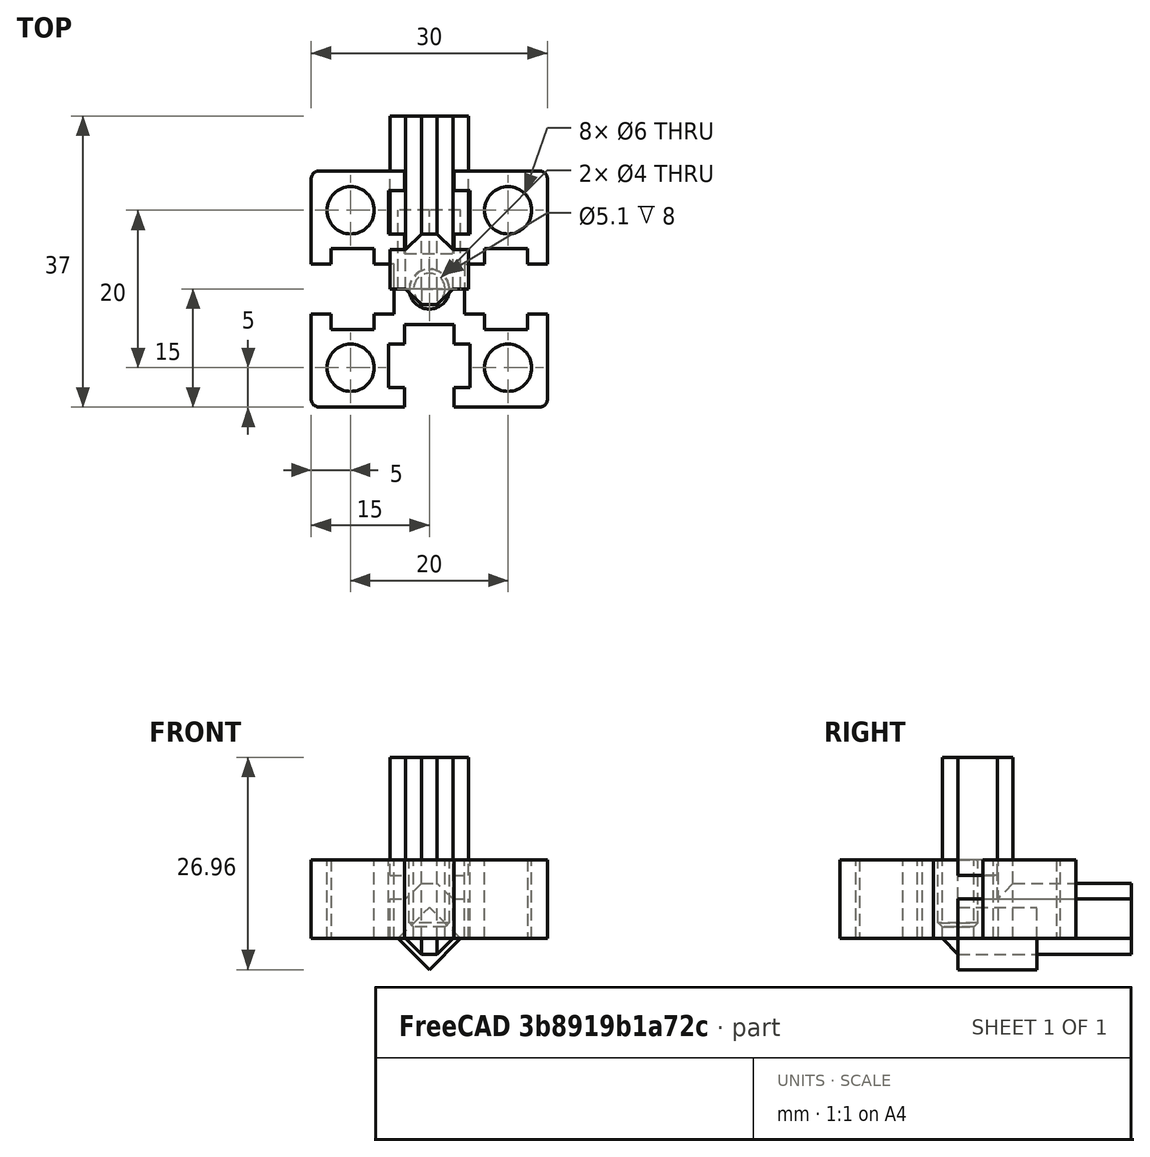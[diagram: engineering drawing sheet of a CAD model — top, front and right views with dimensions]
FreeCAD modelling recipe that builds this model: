
FCSTD DOCUMENT  (FreeCAD 0.18R16146 (Git))
Label: 3030-extrusion
License: All rights reserved
LicenseURL: http://en.wikipedia.org/wiki/All_rights_reserved
objects: Part::Feature×7, Part::Cylinder×6, Part::Box×5, Part::Chamfer×3, Part::MultiFuse×2, Part::Cut×2, Part::Fillet×1
note: 26 computed .brp shape members not serialized (recipe doc carries the construction recipe); baked Part::Feature solids carry a one-line shape summary decoded from their .brp

FEATURE [Part::Box] Box002  label="Cube002"
  AttacherType = Attacher::AttachEngine3D
  Height = 10
  Length = 30
  Placement = pos=(-15,-15,0) rot=(0,0,1;0rad)
  Width = 30
FEATURE [Part::Feature] Fusion001
  Placement = pos=(0,4.5,0) rot=(0,0,1;0rad)
  shape: bbox 10.3 x 10.5 x 10 mm, 22 faces (baked)
FEATURE [Part::Feature] Fusion002
  Placement = pos=(4.5,-1.1e-15,0) rot=(0,0,-1;1.5708rad)
  shape: bbox 10.5 x 10.3 x 10 mm, 22 faces (baked)
FEATURE [Part::Feature] Fusion003
  Placement = pos=(-1e-15,-4.5,0) rot=(0,0,1;3.14159rad)
  shape: bbox 10.3 x 10.5 x 10 mm, 22 faces (baked)
FEATURE [Part::Feature] Fusion004
  Placement = pos=(-4.5,0,0) rot=(0,0,1;1.5708rad)
  shape: bbox 10.5 x 10.3 x 10 mm, 22 faces (baked)
FEATURE [Part::Cylinder] Cylinder
  Angle = 360
  AttacherType = Attacher::AttachEngine3D
  Height = 10
  Placement = pos=(10,10,0) rot=(0,0,1;0rad)
  Radius = 3
FEATURE [Part::Cylinder] Cylinder001
  Angle = 360
  AttacherType = Attacher::AttachEngine3D
  Height = 10
  Radius = 2
FEATURE [Part::Cylinder] Cylinder002
  Angle = 360
  AttacherType = Attacher::AttachEngine3D
  Height = 10
  Placement = pos=(-10,10,0) rot=(0,0,1;0rad)
  Radius = 3
FEATURE [Part::Cylinder] Cylinder003
  Angle = 360
  AttacherType = Attacher::AttachEngine3D
  Height = 10
  Placement = pos=(10,-10,0) rot=(0,0,1;0rad)
  Radius = 3
FEATURE [Part::Cylinder] Cylinder004
  Angle = 360
  AttacherType = Attacher::AttachEngine3D
  Height = 10
  Placement = pos=(-10,-10,0) rot=(0,0,1;0rad)
  Radius = 3
FEATURE [Part::Feature] Box006001001  label="square-nut-template"
  shape: bbox 7.92 x 10 x 7.92 mm, 6 faces (baked)
FEATURE [Part::Box] Box006001002  label="Cube006"
  AttacherType = Attacher::AttachEngine3D
  Height = 5
  Length = 10
  Width = 22
FEATURE [Part::Box] Box006001003  label="Cube007"
  AttacherType = Attacher::AttachEngine3D
  Height = 15
  Length = 10
  Placement = pos=(0,0,8) rot=(0,0,1;0rad)
  Width = 5
FEATURE [Part::Box] Box006001004  label="Cube008"
  AttacherType = Attacher::AttachEngine3D
  Height = 9
  Length = 6
  Placement = pos=(2,0,-2) rot=(0,0,1;0rad)
  Width = 22
FEATURE [Part::Box] Box006001005  label="Cube009"
  AttacherType = Attacher::AttachEngine3D
  Height = 25
  Length = 6
  Placement = pos=(2,-2,-2) rot=(0,0,1;0rad)
  Width = 9
FEATURE [Part::Chamfer] Chamfer002
  Base = -> Box006001004
  Edges = 4 edges r=2: [Edge2,Edge4,Edge6,Edge8]
FEATURE [Part::Chamfer] Chamfer003
  Base = -> Box006001005
  Edges = 7 edges r=2: [Edge1,Edge3,Edge4,Edge5,Edge7,Edge8,Edge9]
FEATURE [Part::MultiFuse] Fusion006002004
  Placement = pos=(-5,0,0) rot=(0,0,1;0rad)
  Shapes = -> [Box006001002,Chamfer003,Chamfer002,Box006001003]
FEATURE [Part::MultiFuse] Fusion006002006
  Shapes = -> [Cylinder004,Fusion001,Fusion003,Fusion004,Fusion002,Cylinder,Cylinder002,Cylinder001,Cylinder003]
FEATURE [Part::Fillet] Fillet
  Base = -> Box002
  Edges = 4 edges r=1: [Edge1,Edge3,Edge5,Edge7]
FEATURE [Part::Cut] Cut  label="extrusion-template"
  Base = -> Fillet
  Tool = -> Fusion006002006
FEATURE [Part::Feature] Cut001  label="extrusion-template001"
  shape: bbox 30 x 30 x 10 mm, 63 faces (baked)
FEATURE [Part::Cylinder] Cylinder005
  Angle = 360
  AttacherType = Attacher::AttachEngine3D
  Height = 8
  Placement = pos=(0,0,2) rot=(0,0,1;0rad)
  Radius = 2.55
FEATURE [Part::Cut] Cut002
  Base = -> Cut001
  Tool = -> Cylinder005
FEATURE [Part::Chamfer] Chamfer  label="head-tail-base"
  Base = -> Cut002
  Edges = 1 edges r=0.5: [Edge185]
FEATURE [Part::Feature] Cut003_cs  label="Extrusion-cut"
  Placement = pos=(0,0,-5) rot=(0,0,1;0rad)
  shape: bbox 30 x 30 x 3e-07 mm, 0 faces, 0 solids (baked)
